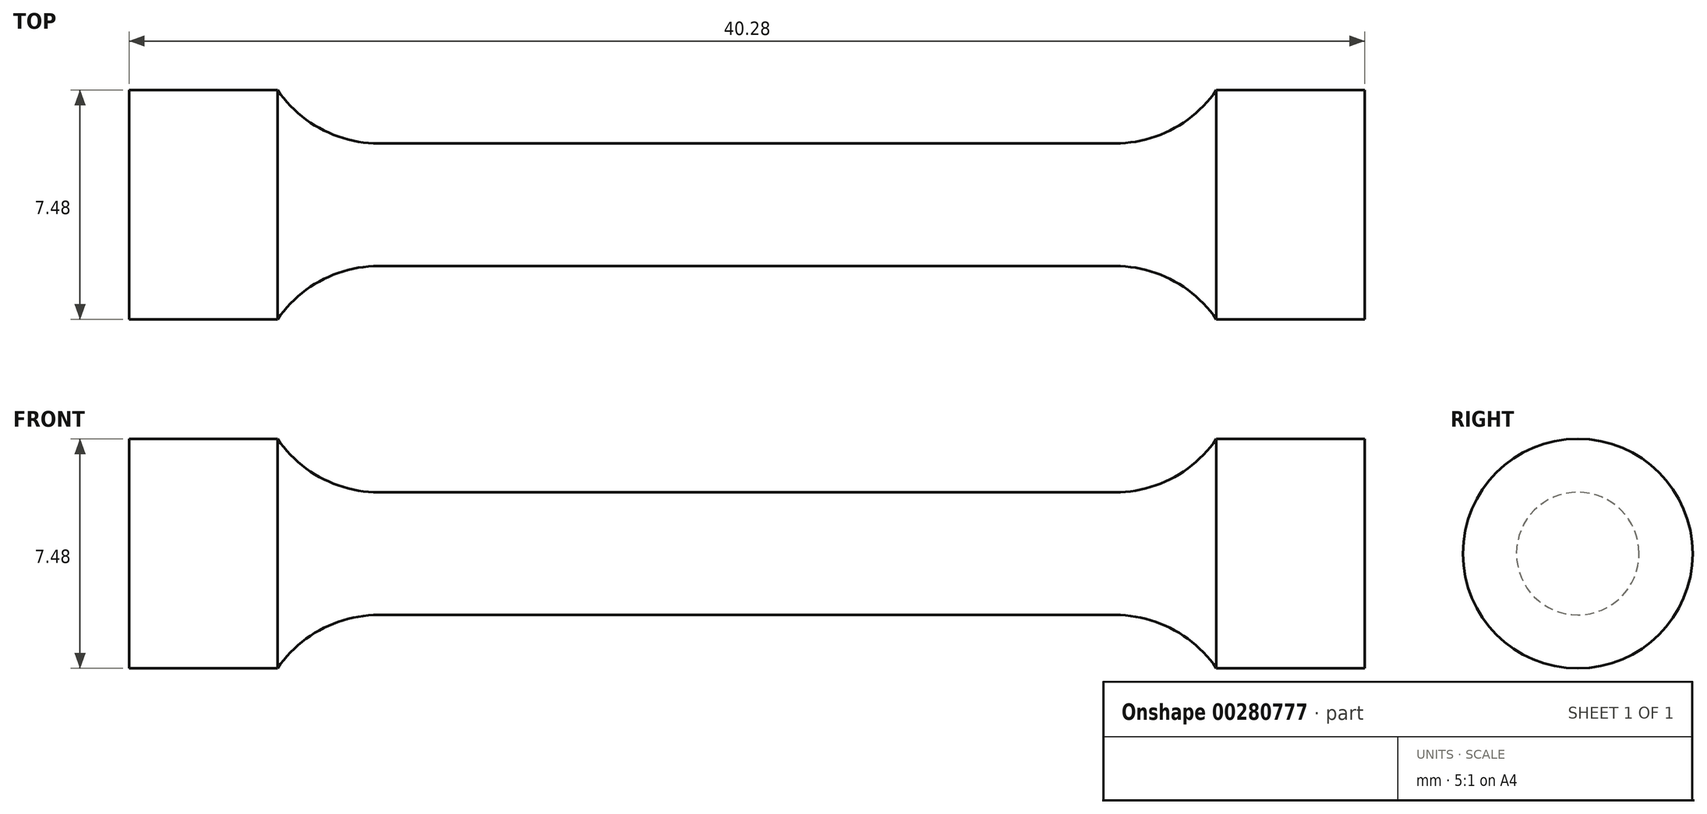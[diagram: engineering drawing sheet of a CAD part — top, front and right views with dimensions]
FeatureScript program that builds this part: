
annotation { "Feature Type Name" : "Feature", "Feature Type Description" : "" }
export const myFeature = defineFeature(function(context is Context, id is Id, definition is map)
    precondition{}
    {
        {
            var Q0;
            Q0=qCreatedBy(makeId("Front.planeOp"),FACE);
            var sketch = newSketch(context, id + "F0", { "sketchPlane" : qUnion([Q0])});
            skLineSegment(sketch, "E0", {"start": v(0, 2) * mm, "end": v(12, 2) * mm});
            skArc(sketch, "E1", {"start": v(12, 2) * mm, "mid": v(13.87, 2.46) * mm, "end": v(15.3, 3.74) * mm});
            skLineSegment(sketch, "E2", {"start": v(15.3, 3.74) * mm, "end": v(20.14, 3.74) * mm});
            skLineSegment(sketch, "E3", {"start": v(20.14, 3.74) * mm, "end": v(20.14, 0) * mm});
            skLineSegment(sketch, "E4.MirrorCS", {"start": v(0, 2) * mm, "end": v(-12, 2) * mm});
            skArc(sketch, "E5.MirrorCS", {"start": v(-12, 2) * mm, "mid": v(-13.87, 2.46) * mm, "end": v(-15.3, 3.74) * mm});
            skLineSegment(sketch, "E6.MirrorCS", {"start": v(-20.14, 3.74) * mm, "end": v(-20.14, 0) * mm});
            skLineSegment(sketch, "E7.MirrorCS", {"start": v(-15.3, 3.74) * mm, "end": v(-20.14, 3.74) * mm});
            skLineSegment(sketch, "E8", {"start": v(-20.14, 0) * mm, "end": v(20.14, 0) * mm});
            skSolve(sketch);
        }
        {
            var Q0;
            Q0=makeQuery(id+"F0.imprint","IMPRINT",FACE,{"disambiguationData":[TD([[makeQuery(id+"F0.imprint","IMPRINT",EDGE,{"derivedFrom":sQuery(id+"F0.wireOp",EDGE,"E0")}),-1.0]])]});
            var Q1;
            Q1=sQuery(id+"F0.wireOp",EDGE,"E8");
            revolve(context, id + "F1", {"entities" : qUnion([Q0]), "axis" : qUnion([Q1]), "revolveType" : RevolveType.FULL});
        }
    });
